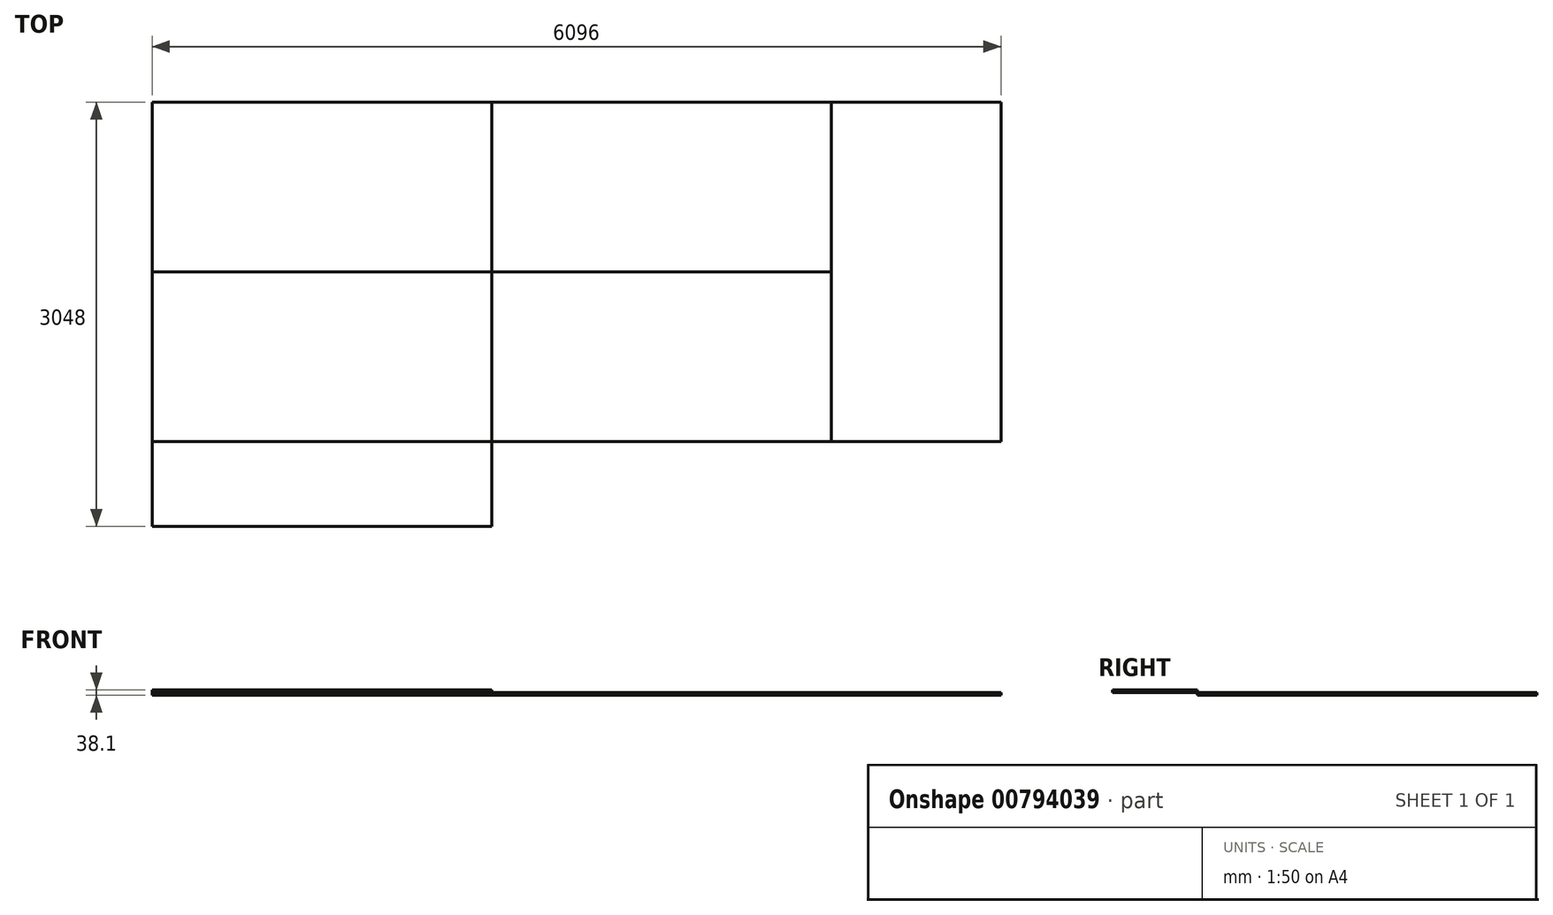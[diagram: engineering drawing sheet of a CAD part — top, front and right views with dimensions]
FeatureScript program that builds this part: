
annotation { "Feature Type Name" : "Feature", "Feature Type Description" : "" }
export const myFeature = defineFeature(function(context is Context, id is Id, definition is map)
    precondition{}
    {
        {
            var Q0;
            Q0=qCreatedBy(makeId("Top.planeOp"),FACE);
            var sketch = newSketch(context, id + "F0", { "sketchPlane" : qUnion([Q0])});
            skLineSegment(sketch, "E0.bottom", {"start": v(-974.61, 632.3) * mm, "end": v(1463.79, 632.3) * mm});
            skLineSegment(sketch, "E0.top", {"start": v(-974.61, -586.9) * mm, "end": v(1463.79, -586.9) * mm});
            skLineSegment(sketch, "E0.left", {"start": v(-974.61, 632.3) * mm, "end": v(-974.61, -586.9) * mm});
            skLineSegment(sketch, "E0.right", {"start": v(1463.79, 632.3) * mm, "end": v(1463.79, -586.9) * mm});
            skSolve(sketch);
        }
        {
            var Q0;
            Q0=makeQuery(id+"F0.imprint","IMPRINT",FACE,{"disambiguationData":[TD([[makeQuery(id+"F0.imprint","IMPRINT",EDGE,{"derivedFrom":sQuery(id+"F0.wireOp",EDGE,"E0.bottom")}),-1.0]])]});
            extrude(context, id + "F1", {"entities" : qUnion([Q0]), "depth" : 19.05 * mm, "offsetDistance" : 25.4 * mm});
        }
        {
            var Q0;
            Q0=makeQuery(id+"F1.opExtrude","SWEPT_BODY",BODY,{"disambiguationData":[OSD([sQuery(id+"F0.wireOp",EDGE,"E0.bottom"),sQuery(id+"F0.wireOp",EDGE,"E0.top"),sQuery(id+"F0.wireOp",EDGE,"E0.left"),sQuery(id+"F0.wireOp",EDGE,"E0.right")])]});
            transform(context, id + "F2", {"entities" : qUnion([Q0]), "transformType" : TransformType.TRANSLATION_3D, "dx" : 0 * mm, "dy" : -1219.2 * mm, "dz" : 0 * mm, "makeCopy" : true});
        }
        {
            var Q0;
            Q0=makeQuery(id+"F2.opPattern","COPY",BODY,{"derivedFrom":makeQuery(id+"F1.opExtrude","SWEPT_BODY",BODY,{"disambiguationData":[OSD([sQuery(id+"F0.wireOp",EDGE,"E0.bottom"),sQuery(id+"F0.wireOp",EDGE,"E0.top"),sQuery(id+"F0.wireOp",EDGE,"E0.left"),sQuery(id+"F0.wireOp",EDGE,"E0.right")])]}),"instanceName":"1"});
            transform(context, id + "F3", {"entities" : qUnion([Q0]), "transformType" : TransformType.TRANSLATION_3D, "dx" : 2438.4 * mm, "dy" : 0 * mm, "dz" : 0 * mm, "makeCopy" : true});
        }
        {
            var Q0;
            Q0=makeQuery(id+"F3.opPattern","COPY",BODY,{"derivedFrom":makeQuery(id+"F2.opPattern","COPY",BODY,{"derivedFrom":makeQuery(id+"F1.opExtrude","SWEPT_BODY",BODY,{"disambiguationData":[OSD([sQuery(id+"F0.wireOp",EDGE,"E0.bottom"),sQuery(id+"F0.wireOp",EDGE,"E0.top"),sQuery(id+"F0.wireOp",EDGE,"E0.left"),sQuery(id+"F0.wireOp",EDGE,"E0.right")])]}),"instanceName":"1"}),"instanceName":"1"});
            transform(context, id + "F4", {"entities" : qUnion([Q0]), "transformType" : TransformType.TRANSLATION_3D, "dx" : 0 * mm, "dy" : 1219.2 * mm, "dz" : 0 * mm, "makeCopy" : true});
        }
        {
            var Q0;
            Q0=makeQuery(id+"F4.opPattern","COPY",BODY,{"derivedFrom":makeQuery(id+"F3.opPattern","COPY",BODY,{"derivedFrom":makeQuery(id+"F2.opPattern","COPY",BODY,{"derivedFrom":makeQuery(id+"F1.opExtrude","SWEPT_BODY",BODY,{"disambiguationData":[OSD([sQuery(id+"F0.wireOp",EDGE,"E0.bottom"),sQuery(id+"F0.wireOp",EDGE,"E0.top"),sQuery(id+"F0.wireOp",EDGE,"E0.left"),sQuery(id+"F0.wireOp",EDGE,"E0.right")])]}),"instanceName":"1"}),"instanceName":"1"}),"instanceName":"1"});
            transform(context, id + "F5", {"entities" : qUnion([Q0]), "transformType" : TransformType.TRANSLATION_3D, "dx" : 2438.4 * mm, "dy" : 0 * mm, "dz" : 0 * mm, "makeCopy" : true});
        }
        {
            var Q0;
            Q0=makeQuery(id+"F5.opPattern","COPY",BODY,{"derivedFrom":makeQuery(id+"F4.opPattern","COPY",BODY,{"derivedFrom":makeQuery(id+"F3.opPattern","COPY",BODY,{"derivedFrom":makeQuery(id+"F2.opPattern","COPY",BODY,{"derivedFrom":makeQuery(id+"F1.opExtrude","SWEPT_BODY",BODY,{"disambiguationData":[OSD([sQuery(id+"F0.wireOp",EDGE,"E0.bottom"),sQuery(id+"F0.wireOp",EDGE,"E0.top"),sQuery(id+"F0.wireOp",EDGE,"E0.left"),sQuery(id+"F0.wireOp",EDGE,"E0.right")])]}),"instanceName":"1"}),"instanceName":"1"}),"instanceName":"1"}),"instanceName":"1"});
            deleteBodies(context, id + "F6", {"entities" : qUnion([Q0])});
        }
        {
            var Q0;
            Q0=makeQuery(id+"F3.opPattern","COPY",FACE,{"derivedFrom":makeQuery(id+"F2.opPattern","COPY",FACE,{"derivedFrom":makeQuery(id+"F1.opExtrude","CAP_FACE",FACE,{"disambiguationData":[OSD([sQuery(id+"F0.wireOp",EDGE,"E0.bottom"),sQuery(id+"F0.wireOp",EDGE,"E0.top"),sQuery(id+"F0.wireOp",EDGE,"E0.left"),sQuery(id+"F0.wireOp",EDGE,"E0.right")])],"isStart":true}),"instanceName":"1"}),"instanceName":"1"});
            var sketch = newSketch(context, id + "F7", { "sketchPlane" : qUnion([Q0])});
            skLineSegment(sketch, "E1.bottom", {"start": v(3902.19, -632.3) * mm, "end": v(5121.39, -632.3) * mm});
            skLineSegment(sketch, "E1.top", {"start": v(3902.19, 1806.1) * mm, "end": v(5121.39, 1806.1) * mm});
            skLineSegment(sketch, "E1.left", {"start": v(3902.19, -632.3) * mm, "end": v(3902.19, 1806.1) * mm});
            skLineSegment(sketch, "E1.right", {"start": v(5121.39, -632.3) * mm, "end": v(5121.39, 1806.1) * mm});
            skSolve(sketch);
        }
        {
            var Q0;
            {var subQ3=sQuery(id+"F7.wireOp",EDGE,"E1.bottom");Q0=makeQuery(id+"F7.imprint","IMPRINT",FACE,{"disambiguationData":[TD([[makeQuery(id+"F7.imprint","IMPRINT",EDGE,{"derivedFrom":subQ3}),1.0]])]});}
            extrude(context, id + "F8", {"entities" : qUnion([Q0]), "oppositeDirection" : true, "depth" : 19.05 * mm, "offsetDistance" : 25.4 * mm});
        }
        {
            var Q0;
            Q0=makeQuery(id+"F2.opPattern","COPY",FACE,{"derivedFrom":makeQuery(id+"F1.opExtrude","CAP_FACE",FACE,{"disambiguationData":[OSD([sQuery(id+"F0.wireOp",EDGE,"E0.bottom"),sQuery(id+"F0.wireOp",EDGE,"E0.top"),sQuery(id+"F0.wireOp",EDGE,"E0.left"),sQuery(id+"F0.wireOp",EDGE,"E0.right")])],"isStart":false}),"instanceName":"1"});
            var sketch = newSketch(context, id + "F9", { "sketchPlane" : qUnion([Q0])});
            skLineSegment(sketch, "E2.bottom", {"start": v(-974.61, -1806.1) * mm, "end": v(1463.79, -1806.1) * mm});
            skLineSegment(sketch, "E2.top", {"start": v(-974.61, -2415.7) * mm, "end": v(1463.79, -2415.7) * mm});
            skLineSegment(sketch, "E2.left", {"start": v(-974.61, -1806.1) * mm, "end": v(-974.61, -2415.7) * mm});
            skLineSegment(sketch, "E2.right", {"start": v(1463.79, -1806.1) * mm, "end": v(1463.79, -2415.7) * mm});
            skSolve(sketch);
        }
        {
            var Q0;
            Q0=makeQuery(id+"F9.imprint","IMPRINT",FACE,{"disambiguationData":[TD([[makeQuery(id+"F9.imprint","IMPRINT",EDGE,{"derivedFrom":sQuery(id+"F9.wireOp",EDGE,"E2.bottom")}),-1.0]])]});
            extrude(context, id + "F10", {"entities" : qUnion([Q0]), "depth" : 19.05 * mm, "offsetDistance" : 25.4 * mm});
        }
    });
